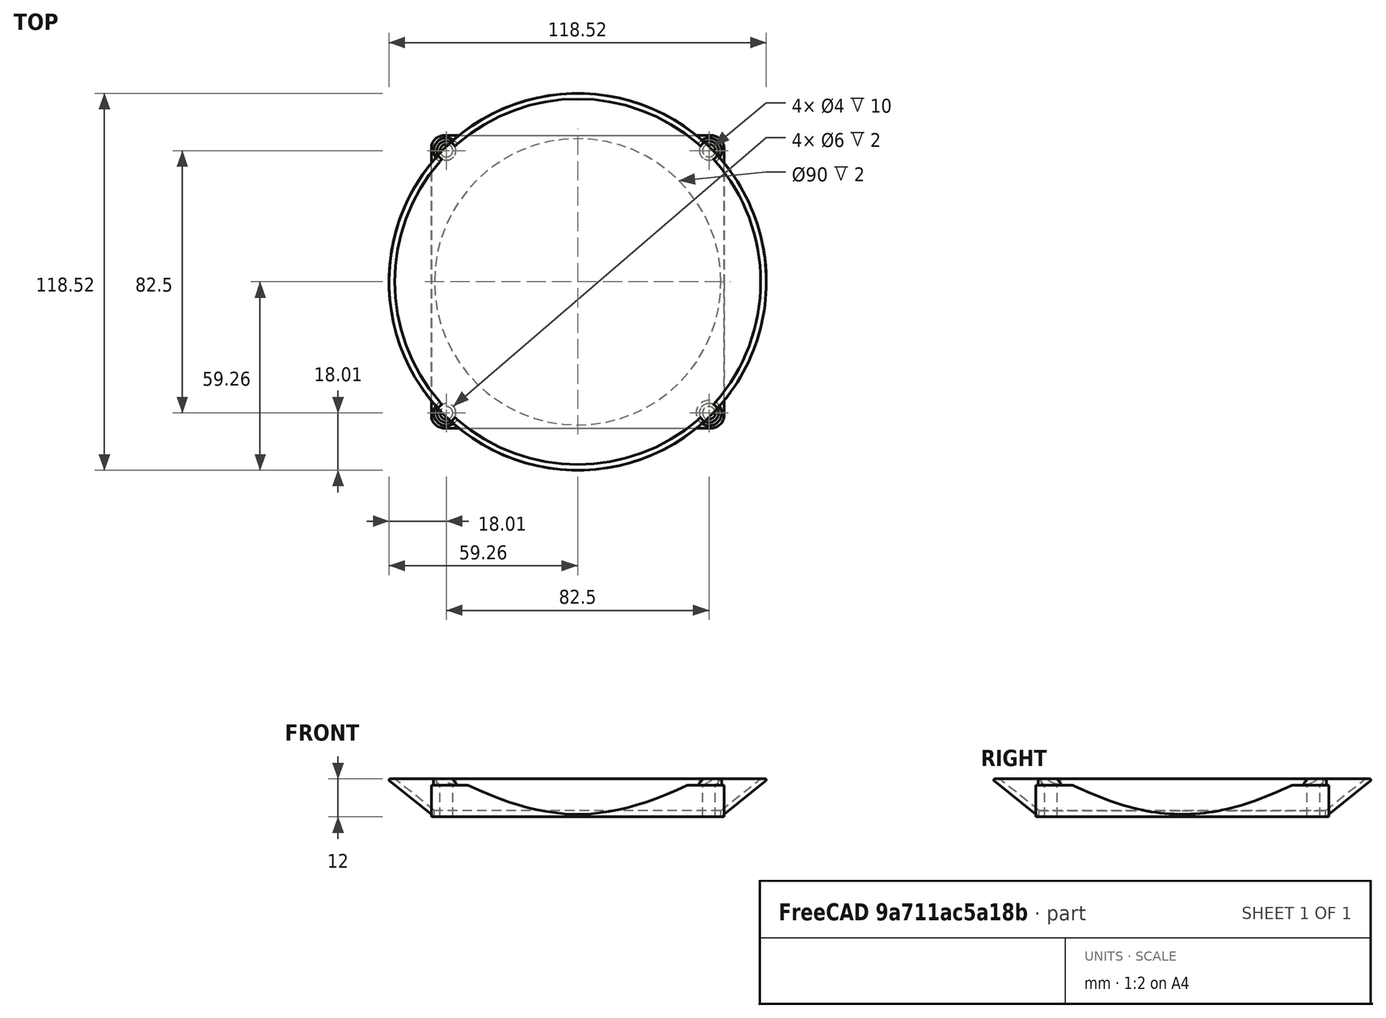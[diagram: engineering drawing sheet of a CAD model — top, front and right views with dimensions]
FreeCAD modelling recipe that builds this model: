
FCSTD DOCUMENT  (FreeCAD 0.18R16117 (Git))
Label: fan duct v2
License: All rights reserved
LicenseURL: http://en.wikipedia.org/wiki/All_rights_reserved
objects: Part::Cylinder×13, Part::MultiFuse×5, Part::Cut×3, Part::Fillet×3, Part::Cone×2, Part::Box×1
note: 27 computed .brp shape members not serialized (recipe doc carries the construction recipe); baked Part::Feature solids carry a one-line shape summary decoded from their .brp

FEATURE [Part::Box] Box  label="Cube"
  AttacherType = Attacher::AttachEngine3D
  Height = 10
  Length = 92
  Placement = pos=(-46,-46,0) rot=(0,0,1;0rad)
  Width = 92
FEATURE [Part::Cone] Cone
  Angle = 360
  AttacherType = Attacher::AttachEngine3D
  Height = 12
  Radius1 = 45
  Radius2 = 60
FEATURE [Part::Cone] Cone001
  Angle = 360
  AttacherType = Attacher::AttachEngine3D
  Height = 12
  Placement = pos=(0,0,2) rot=(0,0,1;0rad)
  Radius1 = 45
  Radius2 = 60
FEATURE [Part::Cylinder] Cylinder
  Angle = 360
  AttacherType = Attacher::AttachEngine3D
  Height = 18
  Placement = pos=(0,0,-3) rot=(0,0,1;0rad)
  Radius = 45
FEATURE [Part::MultiFuse] Fusion  label="Void"
  Shapes = -> [Cylinder,Cone001]
FEATURE [Part::MultiFuse] Fusion001  label="Main"
  Shapes = -> [Cone,Box]
FEATURE [Part::Cylinder] Cylinder001
  Angle = 360
  AttacherType = Attacher::AttachEngine3D
  Height = 12
  Placement = pos=(41.25,41.25,0) rot=(0,0,1;0rad)
  Radius = 4
FEATURE [Part::Cylinder] Cylinder002
  Angle = 360
  AttacherType = Attacher::AttachEngine3D
  Height = 12
  Placement = pos=(-41.25,41.25,0) rot=(0,0,1;0rad)
  Radius = 4
FEATURE [Part::Cylinder] Cylinder003
  Angle = 360
  AttacherType = Attacher::AttachEngine3D
  Height = 12
  Placement = pos=(41.25,-41.25,0) rot=(0,0,1;0rad)
  Radius = 4
FEATURE [Part::Cylinder] Cylinder004
  Angle = 360
  AttacherType = Attacher::AttachEngine3D
  Height = 12
  Placement = pos=(-41.25,-41.25,0) rot=(0,0,1;0rad)
  Radius = 4
FEATURE [Part::MultiFuse] Fusion002
  Shapes = -> [Cylinder001,Cylinder002,Cylinder004,Cylinder003,Fusion001]
FEATURE [Part::Cylinder] Cylinder005
  Angle = 360
  AttacherType = Attacher::AttachEngine3D
  Height = 12
  Placement = pos=(41.25,41.25,0) rot=(0,0,1;0rad)
  Radius = 2
FEATURE [Part::Cylinder] Cylinder006
  Angle = 360
  AttacherType = Attacher::AttachEngine3D
  Height = 12
  Placement = pos=(-41.25,41.25,0) rot=(0,0,1;0rad)
  Radius = 2
FEATURE [Part::Cylinder] Cylinder007
  Angle = 360
  AttacherType = Attacher::AttachEngine3D
  Height = 12
  Placement = pos=(-41.25,-41.25,0) rot=(0,0,1;0rad)
  Radius = 2
FEATURE [Part::Cylinder] Cylinder008
  Angle = 360
  AttacherType = Attacher::AttachEngine3D
  Height = 12
  Placement = pos=(41.25,-41.25,0) rot=(0,0,1;0rad)
  Radius = 2
FEATURE [Part::MultiFuse] Fusion003  label="Screwhole Voids"
  Shapes = -> [Cylinder005,Cylinder008,Cylinder006,Cylinder007]
FEATURE [Part::Cut] Cut
  Base = -> Fusion002
  Tool = -> Fusion003
FEATURE [Part::Cut] Cut001
  Base = -> Cut
  Tool = -> Fusion
FEATURE [Part::Cylinder] Cylinder009
  Angle = 360
  AttacherType = Attacher::AttachEngine3D
  Height = 12
  Placement = pos=(41.25,41.25,10) rot=(0,0,1;0rad)
  Radius = 3
FEATURE [Part::Cylinder] Cylinder010
  Angle = 360
  AttacherType = Attacher::AttachEngine3D
  Height = 12
  Placement = pos=(-41.25,41.25,10) rot=(0,0,1;0rad)
  Radius = 3
FEATURE [Part::Cylinder] Cylinder011
  Angle = 360
  AttacherType = Attacher::AttachEngine3D
  Height = 12
  Placement = pos=(-41.25,-41.25,10) rot=(0,0,1;0rad)
  Radius = 3
FEATURE [Part::Cylinder] Cylinder012
  Angle = 360
  AttacherType = Attacher::AttachEngine3D
  Height = 12
  Placement = pos=(41.25,-41.25,10) rot=(0,0,1;0rad)
  Radius = 3
FEATURE [Part::MultiFuse] Fusion004
  Shapes = -> [Cylinder012,Cylinder009,Cylinder010,Cylinder011]
FEATURE [Part::Cut] Cut002
  Base = -> Cut001
  Tool = -> Fusion004
FEATURE [Part::Fillet] Fillet
  Base = -> Cone
  Edges = 1 edges r=0.4: [Edge1]
FEATURE [Part::Fillet] Fillet001
  Base = -> Cut002
  Edges = 10 edges r=0.4: [Edge4,Edge5,Edge13,Edge19,Edge33,Edge48,Edge93,Edge105,Edge106,Edge128]
FEATURE [Part::Fillet] Fillet002
  Base = -> Fillet001
  Edges = 4 edges r=4: [Edge43,Edge45,Edge50,Edge82]
